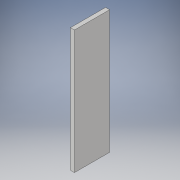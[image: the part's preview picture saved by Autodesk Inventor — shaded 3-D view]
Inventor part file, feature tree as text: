
AUTODESK INVENTOR PART (.ipt)
format: ipt  version: 2017 (Build 210142000, 142)  size: 90,624 bytes
history: native  units: in
note: dims shown in document units (in); Inventor stores cm internally (conversion verified against a paired STEP export)
features: extrude x1, sketch x1
ambient origin geometry x8: Origin, YZ Plane, XZ Plane, XY Plane, X Axis, Y Axis, Z Axis, Center Point
bodies: Solid1 (feature_tree)
feature tree (2):
  extrude  "Extrusion1"  Depth=4.345in
  sketch  "Sketch1"  dims[d0=15.28in d1=4.345in d2=0.5in d3=0.0in]
